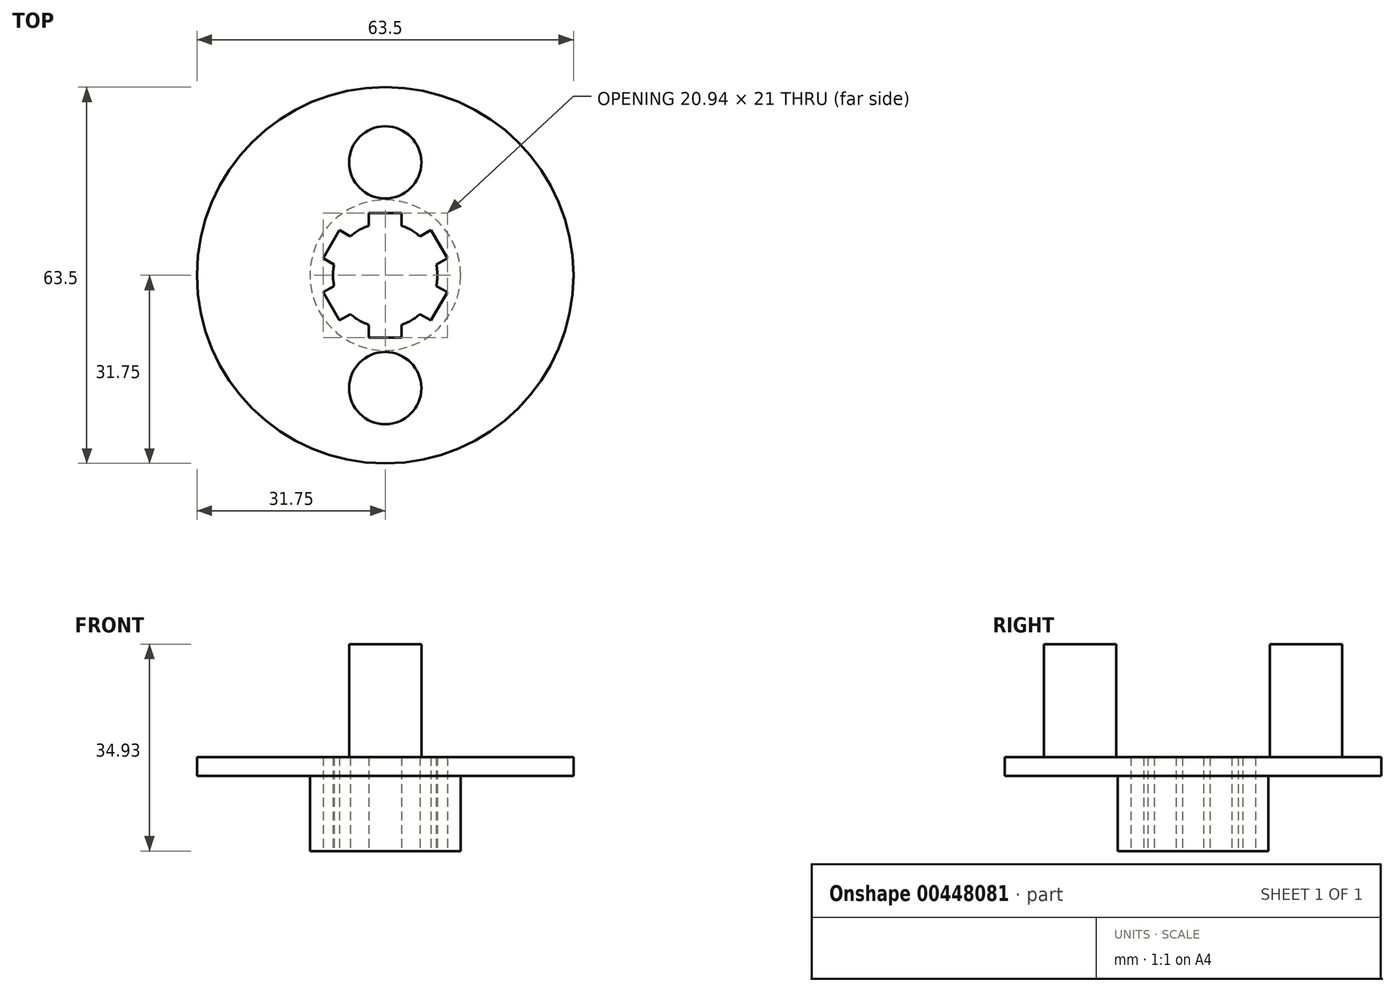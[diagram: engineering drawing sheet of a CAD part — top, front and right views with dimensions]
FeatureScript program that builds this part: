
annotation { "Feature Type Name" : "Feature", "Feature Type Description" : "" }
export const myFeature = defineFeature(function(context is Context, id is Id, definition is map)
    precondition{}
    {
        {
            var Q0;
            Q0=qCreatedBy(makeId("Top.planeOp"),FACE);
            var sketch = newSketch(context, id + "F0", { "sketchPlane" : qUnion([Q0])});
            skCircle(sketch, "E0", {"center": v(0, 0) * mm, "radius": 8.8 * mm});
            skLineSegment(sketch, "E1.bottom", {"start": v(-2.75, 10.5) * mm, "end": v(2.75, 10.5) * mm});
            skLineSegment(sketch, "E1.top", {"start": v(-2.75, 7.5) * mm, "end": v(2.75, 7.5) * mm});
            skLineSegment(sketch, "E1.left", {"start": v(-2.75, 10.5) * mm, "end": v(-2.75, 7.5) * mm});
            skLineSegment(sketch, "E1.right", {"start": v(2.75, 10.5) * mm, "end": v(2.75, 7.5) * mm});
            skPoint(sketch, "E1.middle", {"position": v(0, 9) * mm});
            skLineSegment(sketch, "E2.1.0", {"start": v(-10.47, 2.87) * mm, "end": v(-7.72, 7.63) * mm});
            skLineSegment(sketch, "E2.1.1", {"start": v(-7.72, 7.63) * mm, "end": v(-5.12, 6.13) * mm});
            skLineSegment(sketch, "E2.1.2", {"start": v(-7.87, 1.37) * mm, "end": v(-5.12, 6.13) * mm});
            skLineSegment(sketch, "E2.1.3", {"start": v(-10.47, 2.87) * mm, "end": v(-7.87, 1.37) * mm});
            skLineSegment(sketch, "E2.2.0", {"start": v(-7.72, -7.63) * mm, "end": v(-10.47, -2.87) * mm});
            skLineSegment(sketch, "E2.2.1", {"start": v(-10.47, -2.87) * mm, "end": v(-7.87, -1.37) * mm});
            skLineSegment(sketch, "E2.2.2", {"start": v(-5.12, -6.13) * mm, "end": v(-7.87, -1.37) * mm});
            skLineSegment(sketch, "E2.2.3", {"start": v(-7.72, -7.63) * mm, "end": v(-5.12, -6.13) * mm});
            skLineSegment(sketch, "E2.3.0", {"start": v(2.75, -10.5) * mm, "end": v(-2.75, -10.5) * mm});
            skLineSegment(sketch, "E2.3.1", {"start": v(-2.75, -10.5) * mm, "end": v(-2.75, -7.5) * mm});
            skLineSegment(sketch, "E2.3.2", {"start": v(2.75, -7.5) * mm, "end": v(-2.75, -7.5) * mm});
            skLineSegment(sketch, "E2.3.3", {"start": v(2.75, -10.5) * mm, "end": v(2.75, -7.5) * mm});
            skLineSegment(sketch, "E2.4.0", {"start": v(10.47, -2.87) * mm, "end": v(7.72, -7.63) * mm});
            skLineSegment(sketch, "E2.4.1", {"start": v(7.72, -7.63) * mm, "end": v(5.12, -6.13) * mm});
            skLineSegment(sketch, "E2.4.2", {"start": v(7.87, -1.37) * mm, "end": v(5.12, -6.13) * mm});
            skLineSegment(sketch, "E2.4.3", {"start": v(10.47, -2.87) * mm, "end": v(7.87, -1.37) * mm});
            skLineSegment(sketch, "E2.5.0", {"start": v(7.72, 7.63) * mm, "end": v(10.47, 2.87) * mm});
            skLineSegment(sketch, "E2.5.1", {"start": v(10.47, 2.87) * mm, "end": v(7.87, 1.37) * mm});
            skLineSegment(sketch, "E2.5.2", {"start": v(5.12, 6.13) * mm, "end": v(7.87, 1.37) * mm});
            skLineSegment(sketch, "E2.5.3", {"start": v(7.72, 7.63) * mm, "end": v(5.12, 6.13) * mm});
            skCircle(sketch, "E3", {"center": v(0, 0) * mm, "radius": 12.7 * mm});
            skSolve(sketch);
        }
        {
            var Q0;
            Q0=qSketchRegion(id+"F0",true);
            extrude(context, id + "F1", {"entities" : qUnion([Q0]), "depth" : 12.7 * mm});
        }
        {
            var Q0;
            Q0=makeQuery(id+"F1.opExtrude","CAP_FACE",FACE,{"disambiguationData":[OSD([sQuery(id+"F0.wireOp",EDGE,"E0"),sQuery(id+"F0.wireOp",EDGE,"E1.bottom"),sQuery(id+"F0.wireOp",EDGE,"E1.left"),sQuery(id+"F0.wireOp",EDGE,"E1.right"),sQuery(id+"F0.wireOp",EDGE,"E2.1.0"),sQuery(id+"F0.wireOp",EDGE,"E2.1.1"),sQuery(id+"F0.wireOp",EDGE,"E2.1.3"),sQuery(id+"F0.wireOp",EDGE,"E2.2.0"),sQuery(id+"F0.wireOp",EDGE,"E2.2.1"),sQuery(id+"F0.wireOp",EDGE,"E2.2.3"),sQuery(id+"F0.wireOp",EDGE,"E2.3.0"),sQuery(id+"F0.wireOp",EDGE,"E2.3.1"),sQuery(id+"F0.wireOp",EDGE,"E2.3.3"),sQuery(id+"F0.wireOp",EDGE,"E2.4.0"),sQuery(id+"F0.wireOp",EDGE,"E2.4.1"),sQuery(id+"F0.wireOp",EDGE,"E2.4.3"),sQuery(id+"F0.wireOp",EDGE,"E2.5.0"),sQuery(id+"F0.wireOp",EDGE,"E2.5.1"),sQuery(id+"F0.wireOp",EDGE,"E2.5.3"),sQuery(id+"F0.wireOp",EDGE,"E3")])],"isStart":false});
            var sketch = newSketch(context, id + "F2", { "sketchPlane" : qUnion([Q0])});
            skCircle(sketch, "E4", {"center": v(0, 0) * mm, "radius": 12.7 * mm});
            skSolve(sketch);
        }
        {
            var Q0;
            Q0=makeQuery(id+"FoENzoJBI0EndCu_1.opExtrude","CAP_FACE",FACE,{"disambiguationData":[OSD([sQuery(id+"F2.wireOp",EDGE,"E4")])],"isStart":false});
            var sketch = newSketch(context, id + "F3", { "sketchPlane" : qUnion([Q0])});
            skCircle(sketch, "E5.cCircle", {"center": v(0, 0) * mm, "radius": 6.35 * mm, "construction": true});
            skLineSegment(sketch, "E5.0", {"start": v(-3.67, 6.35) * mm, "end": v(3.67, 6.35) * mm});
            skLineSegment(sketch, "E5.1", {"start": v(3.67, 6.35) * mm, "end": v(7.33, 0) * mm});
            skLineSegment(sketch, "E5.2", {"start": v(7.33, 0) * mm, "end": v(3.67, -6.35) * mm});
            skLineSegment(sketch, "E5.3", {"start": v(3.67, -6.35) * mm, "end": v(-3.67, -6.35) * mm});
            skLineSegment(sketch, "E5.4", {"start": v(-3.67, -6.35) * mm, "end": v(-7.33, 0) * mm});
            skLineSegment(sketch, "E5.5", {"start": v(-7.33, 0) * mm, "end": v(-3.67, 6.35) * mm});
            skPoint(sketch, "E5.0.midPoint", {"position": v(0, 6.35) * mm});
            skSolve(sketch);
        }
        {
            var Q0;
            Q0=makeQuery(id+"F1.opExtrude","CAP_FACE",FACE,{"disambiguationData":[OSD([sQuery(id+"F0.wireOp",EDGE,"E0"),sQuery(id+"F0.wireOp",EDGE,"E1.bottom"),sQuery(id+"F0.wireOp",EDGE,"E1.left"),sQuery(id+"F0.wireOp",EDGE,"E1.right"),sQuery(id+"F0.wireOp",EDGE,"E2.1.0"),sQuery(id+"F0.wireOp",EDGE,"E2.1.1"),sQuery(id+"F0.wireOp",EDGE,"E2.1.3"),sQuery(id+"F0.wireOp",EDGE,"E2.2.0"),sQuery(id+"F0.wireOp",EDGE,"E2.2.1"),sQuery(id+"F0.wireOp",EDGE,"E2.2.3"),sQuery(id+"F0.wireOp",EDGE,"E2.3.0"),sQuery(id+"F0.wireOp",EDGE,"E2.3.1"),sQuery(id+"F0.wireOp",EDGE,"E2.3.3"),sQuery(id+"F0.wireOp",EDGE,"E2.4.0"),sQuery(id+"F0.wireOp",EDGE,"E2.4.1"),sQuery(id+"F0.wireOp",EDGE,"E2.4.3"),sQuery(id+"F0.wireOp",EDGE,"E2.5.0"),sQuery(id+"F0.wireOp",EDGE,"E2.5.1"),sQuery(id+"F0.wireOp",EDGE,"E2.5.3"),sQuery(id+"F0.wireOp",EDGE,"E3")])],"isStart":false});
            var sketch = newSketch(context, id + "F4", { "sketchPlane" : qUnion([Q0])});
            skCircle(sketch, "E6", {"center": v(0, 0) * mm, "radius": 31.75 * mm});
            skSolve(sketch);
        }
        {
            var Q0;
            Q0 = qSketchRegion(id + "F4", true);
            extrude(context, id + "F5", {"entities" : qUnion([Q0]), "operationType" : NewBodyOperationType.ADD, "depth" : 3.17 * mm});
        }
        {
            var Q0;
            Q0=makeQuery(id+"F5.opExtrude","CAP_FACE",FACE,{"disambiguationData":[OSD([sQuery(id+"F4.wireOp",EDGE,"E6")])],"isStart":false});
            var sketch = newSketch(context, id + "F6", { "sketchPlane" : qUnion([Q0])});
            skCircle(sketch, "E7", {"center": v(0, 19.05) * mm, "radius": 6.1 * mm});
            skCircle(sketch, "E8.MirrorC", {"center": v(0, -19.05) * mm, "radius": 6.1 * mm});
            skSolve(sketch);
        }
        {
            var Q0;
            Q0 = qSketchRegion(id + "F6", true);
            extrude(context, id + "F7", {"entities" : qUnion([Q0]), "operationType" : NewBodyOperationType.ADD, "depth" : 19.05 * mm});
        }
        {
            var Q0;
            Q0=makeQuery(id+"F5.boolean.opBoolean","SPLIT",FACE,{"disambiguationData":[TD([makeQuery(id+"F1.opExtrude","SWEPT_FACE",FACE,{"disambiguationData":[OSD([sQuery(id+"F0.wireOp",EDGE,"E1.bottom")])]})])],"derivedFrom":makeQuery(id+"F5.opExtrude","CAP_FACE",FACE,{"disambiguationData":[OSD([sQuery(id+"F4.wireOp",EDGE,"E6")])],"isStart":true})});
            extrude(context, id + "F8", {"entities" : qUnion([Q0]), "operationType" : NewBodyOperationType.REMOVE, "oppositeDirection" : true, "depth" : 25.4 * mm});
        }
    });
